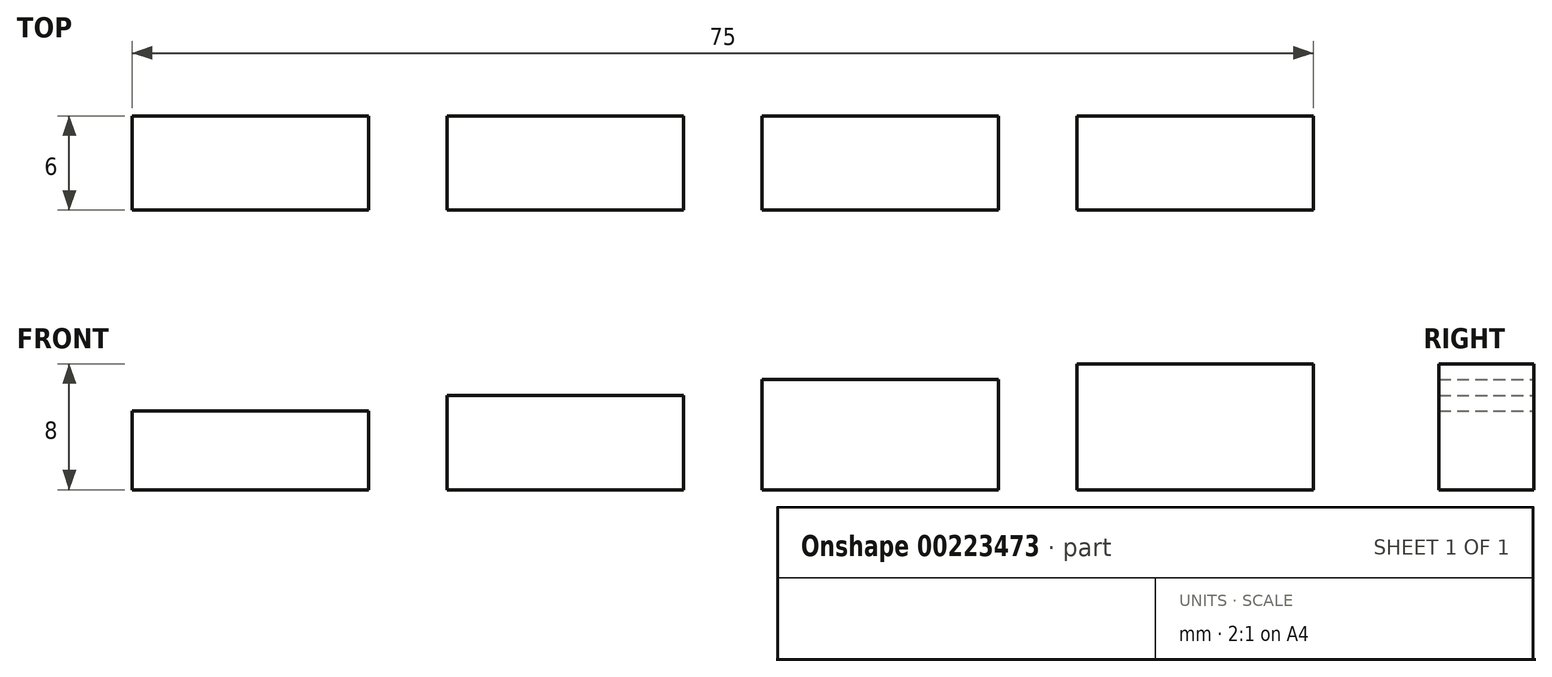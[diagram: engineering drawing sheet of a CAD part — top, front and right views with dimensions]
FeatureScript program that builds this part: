
annotation { "Feature Type Name" : "Feature", "Feature Type Description" : "" }
export const myFeature = defineFeature(function(context is Context, id is Id, definition is map)
    precondition{}
    {
        {
            var Q0;
            Q0=qCreatedBy(makeId("Top.planeOp"),FACE);
            var sketch = newSketch(context, id + "F0", { "sketchPlane" : qUnion([Q0])});
            skLineSegment(sketch, "E0.bottom", {"start": v(0, 0) * mm, "end": v(15, 0) * mm});
            skLineSegment(sketch, "E0.top", {"start": v(0, 6) * mm, "end": v(15, 6) * mm});
            skLineSegment(sketch, "E0.left", {"start": v(0, 0) * mm, "end": v(0, 6) * mm});
            skLineSegment(sketch, "E0.right", {"start": v(15, 0) * mm, "end": v(15, 6) * mm});
            skLineSegment(sketch, "E1.1.0.0", {"start": v(20, 0) * mm, "end": v(35, 0) * mm});
            skLineSegment(sketch, "E1.1.0.1", {"start": v(20, 0) * mm, "end": v(20, 6) * mm});
            skLineSegment(sketch, "E1.1.0.2", {"start": v(20, 6) * mm, "end": v(35, 6) * mm});
            skLineSegment(sketch, "E1.1.0.3", {"start": v(35, 0) * mm, "end": v(35, 6) * mm});
            skLineSegment(sketch, "E1.2.0.0", {"start": v(40, 0) * mm, "end": v(55, 0) * mm});
            skLineSegment(sketch, "E1.2.0.1", {"start": v(40, 0) * mm, "end": v(40, 6) * mm});
            skLineSegment(sketch, "E1.2.0.2", {"start": v(40, 6) * mm, "end": v(55, 6) * mm});
            skLineSegment(sketch, "E1.2.0.3", {"start": v(55, 0) * mm, "end": v(55, 6) * mm});
            skLineSegment(sketch, "E1.3.0.0", {"start": v(60, 0) * mm, "end": v(75, 0) * mm});
            skLineSegment(sketch, "E1.3.0.1", {"start": v(60, 0) * mm, "end": v(60, 6) * mm});
            skLineSegment(sketch, "E1.3.0.2", {"start": v(60, 6) * mm, "end": v(75, 6) * mm});
            skLineSegment(sketch, "E1.3.0.3", {"start": v(75, 0) * mm, "end": v(75, 6) * mm});
            skLineSegment(sketch, "E1.direction1", {"start": v(0, 0) * mm, "end": v(20, 0) * mm, "construction": true});
            skSolve(sketch);
        }
        {
            var Q0;
            Q0=makeQuery(id+"F0.imprint","IMPRINT",FACE,{"disambiguationData":[TD([[makeQuery(id+"F0.imprint","IMPRINT",EDGE,{"derivedFrom":sQuery(id+"F0.wireOp",EDGE,"E0.bottom")}),1.0]])]});
            extrude(context, id + "F1", {"entities" : qUnion([Q0]), "depth" : 5 * mm});
        }
        {
            var Q0;
            Q0=makeQuery(id+"F0.imprint","IMPRINT",FACE,{"disambiguationData":[TD([[makeQuery(id+"F0.imprint","IMPRINT",EDGE,{"derivedFrom":sQuery(id+"F0.wireOp",EDGE,"E1.1.0.0")}),1.0]])]});
            extrude(context, id + "F2", {"entities" : qUnion([Q0]), "depth" : 6 * mm});
        }
        {
            var Q0;
            Q0=makeQuery(id+"F0.imprint","IMPRINT",FACE,{"disambiguationData":[TD([[makeQuery(id+"F0.imprint","IMPRINT",EDGE,{"derivedFrom":sQuery(id+"F0.wireOp",EDGE,"E1.2.0.0")}),1.0]])]});
            extrude(context, id + "F3", {"entities" : qUnion([Q0]), "depth" : 7 * mm});
        }
        {
            var Q0;
            Q0=makeQuery(id+"F0.imprint","IMPRINT",FACE,{"disambiguationData":[TD([[makeQuery(id+"F0.imprint","IMPRINT",EDGE,{"derivedFrom":sQuery(id+"F0.wireOp",EDGE,"E1.3.0.0")}),1.0]])]});
            extrude(context, id + "F4", {"entities" : qUnion([Q0]), "depth" : 8 * mm});
        }
    });
